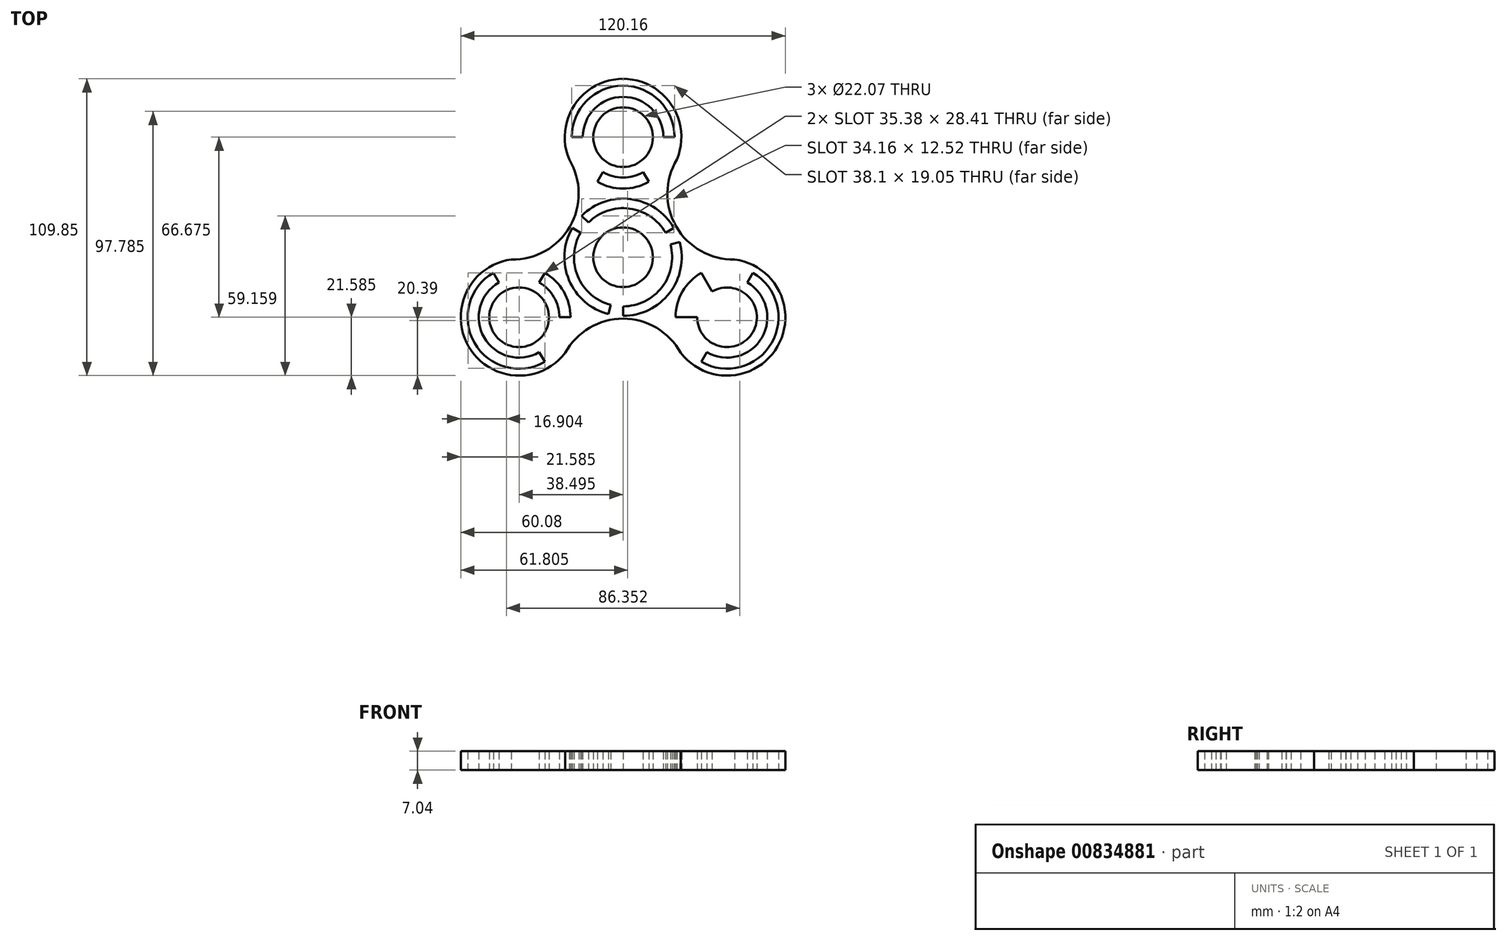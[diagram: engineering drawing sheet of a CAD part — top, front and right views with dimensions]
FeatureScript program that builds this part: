
annotation { "Feature Type Name" : "Feature", "Feature Type Description" : "" }
export const myFeature = defineFeature(function(context is Context, id is Id, definition is map)
    precondition{}
    {
        {
            var Q0;
            Q0=qCreatedBy(makeId("Top.planeOp"),FACE);
            var sketch = newSketch(context, id + "F0", { "sketchPlane" : qUnion([Q0])});
            skCircle(sketch, "E0", {"center": v(0, 0) * mm, "radius": 11.04 * mm});
            skCircle(sketch, "E1", {"center": v(0, 0) * mm, "radius": 14.16 * mm});
            skCircle(sketch, "E2", {"center": v(0, 0) * mm, "radius": 21.71 * mm});
            skLineSegment(sketch, "E3", {"start": v(0, 0) * mm, "end": v(0, 21.71) * mm});
            skLineSegment(sketch, "E4", {"start": v(0, 0) * mm, "end": v(18.8, -10.86) * mm});
            skLineSegment(sketch, "E5", {"start": v(0, 0) * mm, "end": v(-18.8, -10.86) * mm});
            skLineSegment(sketch, "E6", {"start": v(0, 21.71) * mm, "end": v(0, 44.45) * mm});
            skLineSegment(sketch, "E7", {"start": v(18.8, -10.86) * mm, "end": v(38.5, -22.22) * mm});
            skLineSegment(sketch, "E8", {"start": v(-18.8, -10.86) * mm, "end": v(-38.5, -22.22) * mm});
            skLineSegment(sketch, "E9", {"start": v(0, 48.79) * mm, "end": v(0, 44.45) * mm});
            skLineSegment(sketch, "E10", {"start": v(-42.25, -24.4) * mm, "end": v(-38.5, -22.22) * mm});
            skLineSegment(sketch, "E11", {"start": v(42.25, -24.4) * mm, "end": v(38.5, -22.22) * mm});
            skLineSegment(sketch, "E12", {"start": v(-42.25, -24.4) * mm, "end": v(-37.85, -21.85) * mm});
            skLineSegment(sketch, "E13", {"start": v(0, 48.79) * mm, "end": v(0, 43.7) * mm});
            skLineSegment(sketch, "E14", {"start": v(42.25, -24.4) * mm, "end": v(28.65, -16.54) * mm});
            skCircle(sketch, "E15", {"center": v(-38.5, -22.22) * mm, "radius": 11.04 * mm});
            skCircle(sketch, "E16", {"center": v(38.5, -22.22) * mm, "radius": 11.04 * mm});
            skCircle(sketch, "E17", {"center": v(0, 44.45) * mm, "radius": 11.04 * mm});
            skCircle(sketch, "E18", {"center": v(-38.5, -22.22) * mm, "radius": 19.05 * mm});
            skCircle(sketch, "E19", {"center": v(0, 44.45) * mm, "radius": 19.05 * mm});
            skCircle(sketch, "E20", {"center": v(38.5, -22.22) * mm, "radius": 19.05 * mm});
            skLineSegment(sketch, "E21", {"start": v(-38.5, -22.22) * mm, "end": v(-48.02, -5.73) * mm});
            skLineSegment(sketch, "E22", {"start": v(0, 44.45) * mm, "end": v(19.05, 44.45) * mm});
            skLineSegment(sketch, "E23", {"start": v(38.5, -22.22) * mm, "end": v(48.02, -5.73) * mm});
            skLineSegment(sketch, "E24", {"start": v(-38.5, -22.22) * mm, "end": v(-28.97, -38.72) * mm});
            skLineSegment(sketch, "E25", {"start": v(38.5, -22.22) * mm, "end": v(28.97, -38.72) * mm});
            skLineSegment(sketch, "E26", {"start": v(0, 44.45) * mm, "end": v(-19.05, 44.45) * mm});
            skLineSegment(sketch, "E27", {"start": v(0, 0) * mm, "end": v(-18.8, 10.86) * mm});
            skLineSegment(sketch, "E28", {"start": v(-18.8, 10.86) * mm, "end": v(0, 0) * mm});
            skLineSegment(sketch, "E29", {"start": v(0, 0) * mm, "end": v(-10.86, -18.8) * mm});
            skLineSegment(sketch, "E30", {"start": v(-10.86, -18.8) * mm, "end": v(0, 0) * mm});
            skLineSegment(sketch, "E31", {"start": v(0, 0) * mm, "end": v(10.86, -18.8) * mm});
            skLineSegment(sketch, "E32", {"start": v(10.86, -18.8) * mm, "end": v(0, 0) * mm});
            skLineSegment(sketch, "E33", {"start": v(0, 0) * mm, "end": v(10.86, 18.8) * mm});
            skLineSegment(sketch, "E34", {"start": v(10.86, 18.8) * mm, "end": v(0, 0) * mm});
            skLineSegment(sketch, "E35", {"start": v(0, 0) * mm, "end": v(21.71, 0) * mm});
            skLineSegment(sketch, "E36", {"start": v(21.71, 0) * mm, "end": v(0, 0) * mm});
            skLineSegment(sketch, "E37", {"start": v(0, 0) * mm, "end": v(-21.71, 0) * mm});
            skLineSegment(sketch, "E38", {"start": v(-21.71, 0) * mm, "end": v(0, 0) * mm});
            skLineSegment(sketch, "E39", {"start": v(0, 0) * mm, "end": v(-10.86, 18.8) * mm});
            skLineSegment(sketch, "E40", {"start": v(0, 0) * mm, "end": v(18.8, 10.86) * mm});
            skLineSegment(sketch, "E41", {"start": v(0, 0) * mm, "end": v(0, -21.71) * mm});
            skLineSegment(sketch, "E42", {"start": v(0, 0) * mm, "end": v(5.43, 21.02) * mm});
            skPoint(sketch, "E42.endSnap0", {"position": v(5.43, 9.4) * mm});
            skLineSegment(sketch, "E43", {"start": v(0, 0) * mm, "end": v(20.97, 5.62) * mm});
            skLineSegment(sketch, "E44", {"start": v(0, 0) * mm, "end": v(15.35, -15.35) * mm});
            skLineSegment(sketch, "E45", {"start": v(0, 0) * mm, "end": v(-5.43, -21.02) * mm});
            skPoint(sketch, "E45.endSnap0", {"position": v(-5.43, -9.4) * mm});
            skLineSegment(sketch, "E46", {"start": v(0, 0) * mm, "end": v(-20.97, -5.62) * mm});
            skLineSegment(sketch, "E47", {"start": v(0, 0) * mm, "end": v(-15.35, 15.35) * mm});
            skCircle(sketch, "E48", {"center": v(0, 0) * mm, "radius": 24.25 * mm});
            skCircle(sketch, "E49", {"center": v(38.5, -22.22) * mm, "radius": 21.59 * mm});
            skCircle(sketch, "E50", {"center": v(0, 44.45) * mm, "radius": 21.59 * mm});
            skCircle(sketch, "E51", {"center": v(-38.5, -22.22) * mm, "radius": 21.59 * mm});
            skCircle(sketch, "E52", {"center": v(0, 0) * mm, "radius": 18.18 * mm});
            skPoint(sketch, "E53", {"position": v(-19.05, 44.45) * mm});
            skPoint(sketch, "E54", {"position": v(17.11, 36.08) * mm});
            skPoint(sketch, "E55", {"position": v(39.8, -3.22) * mm});
            skPoint(sketch, "E56", {"position": v(22.7, -32.86) * mm});
            skPoint(sketch, "E57", {"position": v(-22.7, -32.86) * mm});
            skPoint(sketch, "E58", {"position": v(-35.27, -0.88) * mm});
            skLineSegment(sketch, "E59", {"start": v(-38.5, -22.22) * mm, "end": v(0, 44.45) * mm});
            skLineSegment(sketch, "E60", {"start": v(0, 44.45) * mm, "end": v(38.5, -22.22) * mm});
            skLineSegment(sketch, "E61", {"start": v(-38.5, -22.22) * mm, "end": v(38.5, -22.22) * mm});
            skLineSegment(sketch, "E62", {"start": v(18.8, 10.86) * mm, "end": v(40.8, 23.56) * mm});
            skLineSegment(sketch, "E63", {"start": v(-18.8, 10.86) * mm, "end": v(-40.8, 23.56) * mm});
            skLineSegment(sketch, "E64", {"start": v(0, -21.71) * mm, "end": v(0, -47.11) * mm});
            skCircle(sketch, "E65", {"center": v(40.8, 23.56) * mm, "radius": 24.38 * mm});
            skCircle(sketch, "E66", {"center": v(0, -47.11) * mm, "radius": 24.38 * mm});
            skCircle(sketch, "E67", {"center": v(-40.8, 23.56) * mm, "radius": 24.38 * mm});
            skCircle(sketch, "E68", {"center": v(-38.5, -22.22) * mm, "radius": 14.92 * mm});
            skCircle(sketch, "E69", {"center": v(38.5, -22.22) * mm, "radius": 14.92 * mm});
            skCircle(sketch, "E70", {"center": v(0, 44.45) * mm, "radius": 14.92 * mm});
            skSolve(sketch);
        }
        {
            var Q0;
            {var subQ0=sQuery(id+"F0.wireOp",EDGE,"E28");var subQ1=sQuery(id+"F0.wireOp",EDGE,"E0");var subQ2=makeQuery(id+"F0.imprint","INTERSECT",VERTEX,{"derivedFrom":[subQ1,subQ0]});Q0=makeQuery(id+"F0.imprint","IMPRINT",FACE,{"disambiguationData":[TD([[makeQuery(id+"F0.imprint","IMPRINT",EDGE,{"disambiguationData":[TD([[subQ2,-1.0]])],"derivedFrom":subQ1}),-1.0]])]});}
            var Q1;
            {var subQ0=sQuery(id+"F0.wireOp",EDGE,"E47");var subQ1=sQuery(id+"F0.wireOp",EDGE,"E0");var subQ2=makeQuery(id+"F0.imprint","INTERSECT",VERTEX,{"derivedFrom":[subQ1,subQ0]});Q1=makeQuery(id+"F0.imprint","IMPRINT",FACE,{"disambiguationData":[TD([[makeQuery(id+"F0.imprint","IMPRINT",EDGE,{"disambiguationData":[TD([[subQ2,-1.0]])],"derivedFrom":subQ1}),-1.0]])]});}
            var Q2;
            {var subQ0=sQuery(id+"F0.wireOp",EDGE,"E39");var subQ1=sQuery(id+"F0.wireOp",EDGE,"E0");var subQ2=makeQuery(id+"F0.imprint","INTERSECT",VERTEX,{"derivedFrom":[subQ1,subQ0]});Q2=makeQuery(id+"F0.imprint","IMPRINT",FACE,{"disambiguationData":[TD([[makeQuery(id+"F0.imprint","IMPRINT",EDGE,{"disambiguationData":[TD([[subQ2,-1.0]])],"derivedFrom":subQ1}),-1.0]])]});}
            var Q3;
            {var subQ0=sQuery(id+"F0.wireOp",EDGE,"E3");var subQ1=sQuery(id+"F0.wireOp",EDGE,"E0");var subQ2=makeQuery(id+"F0.imprint","INTERSECT",VERTEX,{"derivedFrom":[subQ1,subQ0]});Q3=makeQuery(id+"F0.imprint","IMPRINT",FACE,{"disambiguationData":[TD([[makeQuery(id+"F0.imprint","IMPRINT",EDGE,{"disambiguationData":[TD([[subQ2,-1.0]])],"derivedFrom":subQ1}),-1.0]])]});}
            var Q4;
            {var subQ0=sQuery(id+"F0.wireOp",EDGE,"E42");var subQ1=sQuery(id+"F0.wireOp",EDGE,"E0");var subQ2=makeQuery(id+"F0.imprint","INTERSECT",VERTEX,{"derivedFrom":[subQ1,subQ0]});Q4=makeQuery(id+"F0.imprint","IMPRINT",FACE,{"disambiguationData":[TD([[makeQuery(id+"F0.imprint","IMPRINT",EDGE,{"disambiguationData":[TD([[subQ2,-1.0]])],"derivedFrom":subQ1}),-1.0]])]});}
            var Q5;
            {var subQ0=sQuery(id+"F0.wireOp",EDGE,"E34");var subQ1=sQuery(id+"F0.wireOp",EDGE,"E0");var subQ2=makeQuery(id+"F0.imprint","INTERSECT",VERTEX,{"derivedFrom":[subQ1,subQ0]});Q5=makeQuery(id+"F0.imprint","IMPRINT",FACE,{"disambiguationData":[TD([[makeQuery(id+"F0.imprint","IMPRINT",EDGE,{"disambiguationData":[TD([[subQ2,-1.0]])],"derivedFrom":subQ1}),-1.0]])]});}
            var Q6;
            {var subQ0=sQuery(id+"F0.wireOp",EDGE,"E40");var subQ1=sQuery(id+"F0.wireOp",EDGE,"E0");var subQ2=makeQuery(id+"F0.imprint","INTERSECT",VERTEX,{"derivedFrom":[subQ1,subQ0]});Q6=makeQuery(id+"F0.imprint","IMPRINT",FACE,{"disambiguationData":[TD([[makeQuery(id+"F0.imprint","IMPRINT",EDGE,{"disambiguationData":[TD([[subQ2,-1.0]])],"derivedFrom":subQ1}),-1.0]])]});}
            var Q7;
            {var subQ0=sQuery(id+"F0.wireOp",EDGE,"E43");var subQ1=sQuery(id+"F0.wireOp",EDGE,"E0");var subQ2=makeQuery(id+"F0.imprint","INTERSECT",VERTEX,{"derivedFrom":[subQ1,subQ0]});Q7=makeQuery(id+"F0.imprint","IMPRINT",FACE,{"disambiguationData":[TD([[makeQuery(id+"F0.imprint","IMPRINT",EDGE,{"disambiguationData":[TD([[subQ2,-1.0]])],"derivedFrom":subQ1}),-1.0]])]});}
            var Q8;
            {var subQ0=sQuery(id+"F0.wireOp",EDGE,"E43");var subQ1=sQuery(id+"F0.wireOp",EDGE,"E0");var subQ2=makeQuery(id+"F0.imprint","INTERSECT",VERTEX,{"derivedFrom":[subQ1,subQ0]});Q8=makeQuery(id+"F0.imprint","IMPRINT",FACE,{"disambiguationData":[TD([[makeQuery(id+"F0.imprint","IMPRINT",EDGE,{"disambiguationData":[TD([[subQ2,1.0]])],"derivedFrom":subQ1}),-1.0]])]});}
            var Q9;
            {var subQ0=sQuery(id+"F0.wireOp",EDGE,"E36");var subQ1=sQuery(id+"F0.wireOp",EDGE,"E0");var subQ2=makeQuery(id+"F0.imprint","INTERSECT",VERTEX,{"derivedFrom":[subQ1,subQ0]});Q9=makeQuery(id+"F0.imprint","IMPRINT",FACE,{"disambiguationData":[TD([[makeQuery(id+"F0.imprint","IMPRINT",EDGE,{"disambiguationData":[TD([[subQ2,1.0]])],"derivedFrom":subQ1}),-1.0]])]});}
            var Q10;
            {var subQ0=sQuery(id+"F0.wireOp",EDGE,"E44");var subQ1=sQuery(id+"F0.wireOp",EDGE,"E0");var subQ2=makeQuery(id+"F0.imprint","INTERSECT",VERTEX,{"derivedFrom":[subQ1,subQ0]});Q10=makeQuery(id+"F0.imprint","IMPRINT",FACE,{"disambiguationData":[TD([[makeQuery(id+"F0.imprint","IMPRINT",EDGE,{"disambiguationData":[TD([[subQ2,-1.0]])],"derivedFrom":subQ1}),-1.0]])]});}
            var Q11;
            {var subQ0=sQuery(id+"F0.wireOp",EDGE,"E32");var subQ1=sQuery(id+"F0.wireOp",EDGE,"E0");var subQ2=makeQuery(id+"F0.imprint","INTERSECT",VERTEX,{"derivedFrom":[subQ1,subQ0]});Q11=makeQuery(id+"F0.imprint","IMPRINT",FACE,{"disambiguationData":[TD([[makeQuery(id+"F0.imprint","IMPRINT",EDGE,{"disambiguationData":[TD([[subQ2,-1.0]])],"derivedFrom":subQ1}),-1.0]])]});}
            var Q12;
            {var subQ0=sQuery(id+"F0.wireOp",EDGE,"E41");var subQ1=sQuery(id+"F0.wireOp",EDGE,"E0");var subQ2=makeQuery(id+"F0.imprint","INTERSECT",VERTEX,{"derivedFrom":[subQ1,subQ0]});Q12=makeQuery(id+"F0.imprint","IMPRINT",FACE,{"disambiguationData":[TD([[makeQuery(id+"F0.imprint","IMPRINT",EDGE,{"disambiguationData":[TD([[subQ2,-1.0]])],"derivedFrom":subQ1}),-1.0]])]});}
            var Q13;
            {var subQ0=sQuery(id+"F0.wireOp",EDGE,"E30");var subQ1=sQuery(id+"F0.wireOp",EDGE,"E0");var subQ2=makeQuery(id+"F0.imprint","INTERSECT",VERTEX,{"derivedFrom":[subQ1,subQ0]});Q13=makeQuery(id+"F0.imprint","IMPRINT",FACE,{"disambiguationData":[TD([[makeQuery(id+"F0.imprint","IMPRINT",EDGE,{"disambiguationData":[TD([[subQ2,-1.0]])],"derivedFrom":subQ1}),-1.0]])]});}
            var Q14;
            {var subQ0=sQuery(id+"F0.wireOp",EDGE,"E45");var subQ1=sQuery(id+"F0.wireOp",EDGE,"E0");var subQ2=makeQuery(id+"F0.imprint","INTERSECT",VERTEX,{"derivedFrom":[subQ1,subQ0]});Q14=makeQuery(id+"F0.imprint","IMPRINT",FACE,{"disambiguationData":[TD([[makeQuery(id+"F0.imprint","IMPRINT",EDGE,{"disambiguationData":[TD([[subQ2,-1.0]])],"derivedFrom":subQ1}),-1.0]])]});}
            var Q15;
            {var subQ0=sQuery(id+"F0.wireOp",EDGE,"E5");var subQ1=sQuery(id+"F0.wireOp",EDGE,"E0");var subQ2=makeQuery(id+"F0.imprint","INTERSECT",VERTEX,{"derivedFrom":[subQ1,subQ0]});Q15=makeQuery(id+"F0.imprint","IMPRINT",FACE,{"disambiguationData":[TD([[makeQuery(id+"F0.imprint","IMPRINT",EDGE,{"disambiguationData":[TD([[subQ2,-1.0]])],"derivedFrom":subQ1}),-1.0]])]});}
            var Q16;
            {var subQ0=sQuery(id+"F0.wireOp",EDGE,"E46");var subQ1=sQuery(id+"F0.wireOp",EDGE,"E0");var subQ2=makeQuery(id+"F0.imprint","INTERSECT",VERTEX,{"derivedFrom":[subQ1,subQ0]});Q16=makeQuery(id+"F0.imprint","IMPRINT",FACE,{"disambiguationData":[TD([[makeQuery(id+"F0.imprint","IMPRINT",EDGE,{"disambiguationData":[TD([[subQ2,-1.0]])],"derivedFrom":subQ1}),-1.0]])]});}
            var Q17;
            {var subQ0=sQuery(id+"F0.wireOp",EDGE,"E38");var subQ1=sQuery(id+"F0.wireOp",EDGE,"E0");var subQ2=makeQuery(id+"F0.imprint","INTERSECT",VERTEX,{"derivedFrom":[subQ1,subQ0]});Q17=makeQuery(id+"F0.imprint","IMPRINT",FACE,{"disambiguationData":[TD([[makeQuery(id+"F0.imprint","IMPRINT",EDGE,{"disambiguationData":[TD([[subQ2,-1.0]])],"derivedFrom":subQ1}),-1.0]])]});}
            var Q18;
            {var subQ1=sQuery(id+"F0.wireOp",EDGE,"E2");var subQ3=makeQuery(id+"F0.imprint","INTERSECT",VERTEX,{"derivedFrom":[subQ1,sQuery(id+"F0.wireOp",EDGE,"E36")]});Q18=makeQuery(id+"F0.imprint","IMPRINT",FACE,{"disambiguationData":[TD([[makeQuery(id+"F0.imprint","IMPRINT",EDGE,{"disambiguationData":[TD([[subQ3,-1.0]])],"derivedFrom":subQ1}),-1.0]])]});}
            var Q19;
            {var subQ1=sQuery(id+"F0.wireOp",EDGE,"E2");var subQ4=makeQuery(id+"F0.imprint","INTERSECT",VERTEX,{"derivedFrom":[subQ1,sQuery(id+"F0.wireOp",EDGE,"E39")]});Q19=makeQuery(id+"F0.imprint","IMPRINT",FACE,{"disambiguationData":[TD([[makeQuery(id+"F0.imprint","IMPRINT",EDGE,{"disambiguationData":[TD([[subQ4,-1.0]])],"derivedFrom":subQ1}),-1.0]])]});}
            var Q20;
            {var subQ1=sQuery(id+"F0.wireOp",EDGE,"E2");var subQ4=makeQuery(id+"F0.imprint","INTERSECT",VERTEX,{"derivedFrom":[subQ1,sQuery(id+"F0.wireOp",EDGE,"E30")]});Q20=makeQuery(id+"F0.imprint","IMPRINT",FACE,{"disambiguationData":[TD([[makeQuery(id+"F0.imprint","IMPRINT",EDGE,{"disambiguationData":[TD([[subQ4,-1.0]])],"derivedFrom":subQ1}),-1.0]])]});}
            var Q21;
            {var subQ1=sQuery(id+"F0.wireOp",EDGE,"E2");var subQ5=makeQuery(id+"F0.imprint","INTERSECT",VERTEX,{"derivedFrom":[subQ1,sQuery(id+"F0.wireOp",EDGE,"E32")]});Q21=makeQuery(id+"F0.imprint","IMPRINT",FACE,{"disambiguationData":[TD([[makeQuery(id+"F0.imprint","IMPRINT",EDGE,{"disambiguationData":[TD([[subQ5,-1.0]])],"derivedFrom":subQ1}),-1.0]])]});}
            var Q22;
            {var subQ0=sQuery(id+"F0.wireOp",EDGE,"E23");var subQ1=sQuery(id+"F0.wireOp",EDGE,"E16");var subQ2=makeQuery(id+"F0.imprint","INTERSECT",VERTEX,{"derivedFrom":[subQ1,subQ0]});Q22=makeQuery(id+"F0.imprint","IMPRINT",FACE,{"disambiguationData":[TD([[makeQuery(id+"F0.imprint","IMPRINT",EDGE,{"disambiguationData":[TD([[subQ2,1.0]])],"derivedFrom":subQ1}),-1.0]])]});}
            var Q23;
            {var subQ1=sQuery(id+"F0.wireOp",EDGE,"E14");var subQ7=sQuery(id+"F0.wireOp",EDGE,"E7");var subQ8=makeQuery(id+"F0.imprint","INTERSECT",VERTEX,{"derivedFrom":[subQ7,subQ1]});Q23=makeQuery(id+"F0.imprint","IMPRINT",FACE,{"disambiguationData":[TD([[makeQuery(id+"F0.imprint","IMPRINT",EDGE,{"disambiguationData":[TD([[subQ8,1.0]])],"derivedFrom":subQ7}),1.0]])]});}
            var Q24;
            {var subQ5=sQuery(id+"F0.wireOp",EDGE,"E14");var subQ7=sQuery(id+"F0.wireOp",EDGE,"E7");var subQ8=makeQuery(id+"F0.imprint","INTERSECT",VERTEX,{"derivedFrom":[subQ7,subQ5]});Q24=makeQuery(id+"F0.imprint","IMPRINT",FACE,{"disambiguationData":[TD([[makeQuery(id+"F0.imprint","IMPRINT",EDGE,{"disambiguationData":[TD([[subQ8,1.0]])],"derivedFrom":subQ7}),-1.0]])]});}
            var Q25;
            {var subQ0=sQuery(id+"F0.wireOp",EDGE,"E21");var subQ1=sQuery(id+"F0.wireOp",EDGE,"E15");var subQ2=makeQuery(id+"F0.imprint","INTERSECT",VERTEX,{"derivedFrom":[subQ1,subQ0]});Q25=makeQuery(id+"F0.imprint","IMPRINT",FACE,{"disambiguationData":[TD([[makeQuery(id+"F0.imprint","IMPRINT",EDGE,{"disambiguationData":[TD([[subQ2,-1.0]])],"derivedFrom":subQ1}),-1.0]])]});}
            var Q26;
            {var subQ0=sQuery(id+"F0.wireOp",EDGE,"E26");var subQ1=sQuery(id+"F0.wireOp",EDGE,"E17");var subQ2=makeQuery(id+"F0.imprint","INTERSECT",VERTEX,{"derivedFrom":[subQ1,subQ0]});Q26=makeQuery(id+"F0.imprint","IMPRINT",FACE,{"disambiguationData":[TD([[makeQuery(id+"F0.imprint","IMPRINT",EDGE,{"disambiguationData":[TD([[subQ2,1.0]])],"derivedFrom":subQ1}),-1.0]])]});}
            var Q27;
            {var subQ5=sQuery(id+"F0.wireOp",EDGE,"E19");var subQ8=makeQuery(id+"F0.imprint","INTERSECT",VERTEX,{"derivedFrom":[subQ5,sQuery(id+"F0.wireOp",EDGE,"E22")]});Q27=makeQuery(id+"F0.imprint","IMPRINT",FACE,{"disambiguationData":[TD([[makeQuery(id+"F0.imprint","IMPRINT",EDGE,{"disambiguationData":[TD([[subQ8,-1.0]])],"derivedFrom":subQ5}),-1.0]])]});}
            var Q28;
            {var subQ0=sQuery(id+"F0.wireOp",EDGE,"E20");var subQ1=makeQuery(id+"F0.imprint","INTERSECT",VERTEX,{"derivedFrom":[subQ0,sQuery(id+"F0.wireOp",EDGE,"E23")]});Q28=makeQuery(id+"F0.imprint","IMPRINT",FACE,{"disambiguationData":[TD([[makeQuery(id+"F0.imprint","IMPRINT",EDGE,{"disambiguationData":[TD([[subQ1,-1.0]])],"derivedFrom":subQ0}),-1.0]])]});}
            var Q29;
            {var subQ0=sQuery(id+"F0.wireOp",EDGE,"E51");var subQ1=sQuery(id+"F0.wireOp",EDGE,"E8");var subQ2=makeQuery(id+"F0.imprint","INTERSECT",VERTEX,{"derivedFrom":[subQ1,subQ0]});Q29=makeQuery(id+"F0.imprint","IMPRINT",FACE,{"disambiguationData":[TD([[makeQuery(id+"F0.imprint","IMPRINT",EDGE,{"disambiguationData":[TD([[subQ2,-1.0]])],"derivedFrom":subQ1}),1.0]])]});}
            var Q30;
            {var subQ0=sQuery(id+"F0.wireOp",EDGE,"E51");var subQ1=sQuery(id+"F0.wireOp",EDGE,"E8");var subQ2=makeQuery(id+"F0.imprint","INTERSECT",VERTEX,{"derivedFrom":[subQ1,subQ0]});Q30=makeQuery(id+"F0.imprint","IMPRINT",FACE,{"disambiguationData":[TD([[makeQuery(id+"F0.imprint","IMPRINT",EDGE,{"disambiguationData":[TD([[subQ2,-1.0]])],"derivedFrom":subQ1}),-1.0]])]});}
            var Q31;
            {var subQ1=sQuery(id+"F0.wireOp",EDGE,"E48");var subQ6=sQuery(id+"F0.wireOp",EDGE,"E6");var subQ9=makeQuery(id+"F0.imprint","INTERSECT",VERTEX,{"derivedFrom":[subQ6,subQ1]});Q31=makeQuery(id+"F0.imprint","IMPRINT",FACE,{"disambiguationData":[TD([[makeQuery(id+"F0.imprint","IMPRINT",EDGE,{"disambiguationData":[TD([[subQ9,-1.0]])],"derivedFrom":subQ6}),1.0]])]});}
            var Q32;
            {var subQ0=sQuery(id+"F0.wireOp",EDGE,"E50");var subQ1=sQuery(id+"F0.wireOp",EDGE,"E6");var subQ2=makeQuery(id+"F0.imprint","INTERSECT",VERTEX,{"derivedFrom":[subQ1,subQ0]});Q32=makeQuery(id+"F0.imprint","IMPRINT",FACE,{"disambiguationData":[TD([[makeQuery(id+"F0.imprint","IMPRINT",EDGE,{"disambiguationData":[TD([[subQ2,-1.0]])],"derivedFrom":subQ1}),-1.0]])]});}
            var Q33;
            {var subQ0=sQuery(id+"F0.wireOp",EDGE,"E48");var subQ1=sQuery(id+"F0.wireOp",EDGE,"E6");var subQ2=makeQuery(id+"F0.imprint","INTERSECT",VERTEX,{"derivedFrom":[subQ1,subQ0]});Q33=makeQuery(id+"F0.imprint","IMPRINT",FACE,{"disambiguationData":[TD([[makeQuery(id+"F0.imprint","IMPRINT",EDGE,{"disambiguationData":[TD([[subQ2,-1.0]])],"derivedFrom":subQ1}),-1.0]])]});}
            var Q34;
            {var subQ0=sQuery(id+"F0.wireOp",EDGE,"E50");var subQ1=sQuery(id+"F0.wireOp",EDGE,"E6");var subQ2=makeQuery(id+"F0.imprint","INTERSECT",VERTEX,{"derivedFrom":[subQ1,subQ0]});Q34=makeQuery(id+"F0.imprint","IMPRINT",FACE,{"disambiguationData":[TD([[makeQuery(id+"F0.imprint","IMPRINT",EDGE,{"disambiguationData":[TD([[subQ2,-1.0]])],"derivedFrom":subQ1}),1.0]])]});}
            var Q35;
            {var subQ1=sQuery(id+"F0.wireOp",EDGE,"E48");var subQ5=sQuery(id+"F0.wireOp",EDGE,"E7");var subQ6=makeQuery(id+"F0.imprint","INTERSECT",VERTEX,{"derivedFrom":[subQ5,subQ1]});Q35=makeQuery(id+"F0.imprint","IMPRINT",FACE,{"disambiguationData":[TD([[makeQuery(id+"F0.imprint","IMPRINT",EDGE,{"disambiguationData":[TD([[subQ6,-1.0]])],"derivedFrom":subQ5}),1.0]])]});}
            var Q36;
            {var subQ0=sQuery(id+"F0.wireOp",EDGE,"E49");var subQ1=sQuery(id+"F0.wireOp",EDGE,"E7");var subQ2=makeQuery(id+"F0.imprint","INTERSECT",VERTEX,{"derivedFrom":[subQ1,subQ0]});Q36=makeQuery(id+"F0.imprint","IMPRINT",FACE,{"disambiguationData":[TD([[makeQuery(id+"F0.imprint","IMPRINT",EDGE,{"disambiguationData":[TD([[subQ2,-1.0]])],"derivedFrom":subQ1}),1.0]])]});}
            var Q37;
            {var subQ0=sQuery(id+"F0.wireOp",EDGE,"E50");var subQ1=sQuery(id+"F0.wireOp",EDGE,"E48");var subQ2=makeQuery(id+"F0.imprint","INTERSECT",VERTEX,{"disambiguationData":[OD(1.0)],"derivedFrom":[subQ1,subQ0]});Q37=makeQuery(id+"F0.imprint","IMPRINT",FACE,{"disambiguationData":[TD([[makeQuery(id+"F0.imprint","IMPRINT",EDGE,{"disambiguationData":[TD([[subQ2,-1.0]])],"derivedFrom":subQ1}),-1.0]])]});}
            var Q38;
            {var subQ1=sQuery(id+"F0.wireOp",EDGE,"E48");var subQ5=sQuery(id+"F0.wireOp",EDGE,"E8");var subQ6=makeQuery(id+"F0.imprint","INTERSECT",VERTEX,{"derivedFrom":[subQ5,subQ1]});Q38=makeQuery(id+"F0.imprint","IMPRINT",FACE,{"disambiguationData":[TD([[makeQuery(id+"F0.imprint","IMPRINT",EDGE,{"disambiguationData":[TD([[subQ6,-1.0]])],"derivedFrom":subQ5}),-1.0]])]});}
            var Q39;
            {var subQ5=sQuery(id+"F0.wireOp",EDGE,"E18");var subQ9=makeQuery(id+"F0.imprint","INTERSECT",VERTEX,{"derivedFrom":[subQ5,sQuery(id+"F0.wireOp",EDGE,"E21")]});Q39=makeQuery(id+"F0.imprint","IMPRINT",FACE,{"disambiguationData":[TD([[makeQuery(id+"F0.imprint","IMPRINT",EDGE,{"disambiguationData":[TD([[subQ9,1.0]])],"derivedFrom":subQ5}),-1.0]])]});}
            var Q40;
            {var subQ0=sQuery(id+"F0.wireOp",EDGE,"E51");var subQ1=sQuery(id+"F0.wireOp",EDGE,"E48");var subQ2=makeQuery(id+"F0.imprint","INTERSECT",VERTEX,{"disambiguationData":[OD(1.0)],"derivedFrom":[subQ1,subQ0]});Q40=makeQuery(id+"F0.imprint","IMPRINT",FACE,{"disambiguationData":[TD([[makeQuery(id+"F0.imprint","IMPRINT",EDGE,{"disambiguationData":[TD([[subQ2,-1.0]])],"derivedFrom":subQ1}),-1.0]])]});}
            var Q41;
            {var subQ0=sQuery(id+"F0.wireOp",EDGE,"E48");var subQ1=sQuery(id+"F0.wireOp",EDGE,"E7");var subQ2=makeQuery(id+"F0.imprint","INTERSECT",VERTEX,{"derivedFrom":[subQ1,subQ0]});Q41=makeQuery(id+"F0.imprint","IMPRINT",FACE,{"disambiguationData":[TD([[makeQuery(id+"F0.imprint","IMPRINT",EDGE,{"disambiguationData":[TD([[subQ2,-1.0]])],"derivedFrom":subQ1}),-1.0]])]});}
            var Q42;
            {var subQ0=sQuery(id+"F0.wireOp",EDGE,"E49");var subQ1=sQuery(id+"F0.wireOp",EDGE,"E7");var subQ2=makeQuery(id+"F0.imprint","INTERSECT",VERTEX,{"derivedFrom":[subQ1,subQ0]});Q42=makeQuery(id+"F0.imprint","IMPRINT",FACE,{"disambiguationData":[TD([[makeQuery(id+"F0.imprint","IMPRINT",EDGE,{"disambiguationData":[TD([[subQ2,-1.0]])],"derivedFrom":subQ1}),-1.0]])]});}
            var Q43;
            {var subQ1=sQuery(id+"F0.wireOp",EDGE,"E48");var subQ6=sQuery(id+"F0.wireOp",EDGE,"E8");var subQ9=makeQuery(id+"F0.imprint","INTERSECT",VERTEX,{"derivedFrom":[subQ6,subQ1]});Q43=makeQuery(id+"F0.imprint","IMPRINT",FACE,{"disambiguationData":[TD([[makeQuery(id+"F0.imprint","IMPRINT",EDGE,{"disambiguationData":[TD([[subQ9,-1.0]])],"derivedFrom":subQ6}),1.0]])]});}
            var Q44;
            {var subQ0=sQuery(id+"F0.wireOp",EDGE,"E59");var subQ1=sQuery(id+"F0.wireOp",EDGE,"E48");var subQ2=makeQuery(id+"F0.imprint","INTERSECT",VERTEX,{"disambiguationData":[OD(0.0)],"derivedFrom":[subQ1,subQ0]});Q44=makeQuery(id+"F0.imprint","IMPRINT",FACE,{"disambiguationData":[TD([[makeQuery(id+"F0.imprint","IMPRINT",EDGE,{"disambiguationData":[TD([[subQ2,-1.0]])],"derivedFrom":subQ1}),-1.0]])]});}
            var Q45;
            {var subQ0=sQuery(id+"F0.wireOp",EDGE,"E65");var subQ1=sQuery(id+"F0.wireOp",EDGE,"E48");var subQ2=makeQuery(id+"F0.imprint","INTERSECT",VERTEX,{"disambiguationData":[OD(1.0)],"derivedFrom":[subQ1,subQ0]});Q45=makeQuery(id+"F0.imprint","IMPRINT",FACE,{"disambiguationData":[TD([[makeQuery(id+"F0.imprint","IMPRINT",EDGE,{"disambiguationData":[TD([[subQ2,-1.0]])],"derivedFrom":subQ1}),-1.0]])]});}
            var Q46;
            {var subQ0=sQuery(id+"F0.wireOp",EDGE,"E65");var subQ1=sQuery(id+"F0.wireOp",EDGE,"E48");var subQ2=makeQuery(id+"F0.imprint","INTERSECT",VERTEX,{"disambiguationData":[OD(0.0)],"derivedFrom":[subQ1,subQ0]});Q46=makeQuery(id+"F0.imprint","IMPRINT",FACE,{"disambiguationData":[TD([[makeQuery(id+"F0.imprint","IMPRINT",EDGE,{"disambiguationData":[TD([[subQ2,1.0]])],"derivedFrom":subQ1}),-1.0]])]});}
            var Q47;
            {var subQ1=sQuery(id+"F0.wireOp",EDGE,"E2");var subQ7=makeQuery(id+"F0.imprint","INTERSECT",VERTEX,{"derivedFrom":[subQ1,sQuery(id+"F0.wireOp",EDGE,"E38")]});Q47=makeQuery(id+"F0.imprint","IMPRINT",FACE,{"disambiguationData":[TD([[makeQuery(id+"F0.imprint","IMPRINT",EDGE,{"disambiguationData":[TD([[subQ7,-1.0]])],"derivedFrom":subQ1}),-1.0]])]});}
            var Q48;
            {var subQ0=sQuery(id+"F0.wireOp",EDGE,"E67");var subQ1=sQuery(id+"F0.wireOp",EDGE,"E48");var subQ2=makeQuery(id+"F0.imprint","INTERSECT",VERTEX,{"disambiguationData":[OD(1.0)],"derivedFrom":[subQ1,subQ0]});Q48=makeQuery(id+"F0.imprint","IMPRINT",FACE,{"disambiguationData":[TD([[makeQuery(id+"F0.imprint","IMPRINT",EDGE,{"disambiguationData":[TD([[subQ2,-1.0]])],"derivedFrom":subQ1}),1.0]])]});}
            var Q49;
            {var subQ0=sQuery(id+"F0.wireOp",EDGE,"E59");var subQ1=sQuery(id+"F0.wireOp",EDGE,"E48");var subQ2=makeQuery(id+"F0.imprint","INTERSECT",VERTEX,{"disambiguationData":[OD(0.0)],"derivedFrom":[subQ1,subQ0]});Q49=makeQuery(id+"F0.imprint","IMPRINT",FACE,{"disambiguationData":[TD([[makeQuery(id+"F0.imprint","IMPRINT",EDGE,{"disambiguationData":[TD([[subQ2,-1.0]])],"derivedFrom":subQ1}),1.0]])]});}
            var Q50;
            {var subQ0=sQuery(id+"F0.wireOp",EDGE,"E67");var subQ1=sQuery(id+"F0.wireOp",EDGE,"E48");var subQ2=makeQuery(id+"F0.imprint","INTERSECT",VERTEX,{"disambiguationData":[OD(1.0)],"derivedFrom":[subQ1,subQ0]});Q50=makeQuery(id+"F0.imprint","IMPRINT",FACE,{"disambiguationData":[TD([[makeQuery(id+"F0.imprint","IMPRINT",EDGE,{"disambiguationData":[TD([[subQ2,-1.0]])],"derivedFrom":subQ1}),-1.0]])]});}
            var Q51;
            {var subQ0=sQuery(id+"F0.wireOp",EDGE,"E59");var subQ1=sQuery(id+"F0.wireOp",EDGE,"E48");var subQ2=makeQuery(id+"F0.imprint","INTERSECT",VERTEX,{"disambiguationData":[OD(1.0)],"derivedFrom":[subQ1,subQ0]});Q51=makeQuery(id+"F0.imprint","IMPRINT",FACE,{"disambiguationData":[TD([[makeQuery(id+"F0.imprint","IMPRINT",EDGE,{"disambiguationData":[TD([[subQ2,-1.0]])],"derivedFrom":subQ1}),-1.0]])]});}
            var Q52;
            {var subQ0=sQuery(id+"F0.wireOp",EDGE,"E61");var subQ1=sQuery(id+"F0.wireOp",EDGE,"E48");var subQ2=makeQuery(id+"F0.imprint","INTERSECT",VERTEX,{"disambiguationData":[OD(0.0)],"derivedFrom":[subQ1,subQ0]});Q52=makeQuery(id+"F0.imprint","IMPRINT",FACE,{"disambiguationData":[TD([[makeQuery(id+"F0.imprint","IMPRINT",EDGE,{"disambiguationData":[TD([[subQ2,-1.0]])],"derivedFrom":subQ1}),1.0]])]});}
            var Q53;
            {var subQ0=sQuery(id+"F0.wireOp",EDGE,"E66");var subQ1=sQuery(id+"F0.wireOp",EDGE,"E48");var subQ2=makeQuery(id+"F0.imprint","INTERSECT",VERTEX,{"disambiguationData":[OD(1.0)],"derivedFrom":[subQ1,subQ0]});Q53=makeQuery(id+"F0.imprint","IMPRINT",FACE,{"disambiguationData":[TD([[makeQuery(id+"F0.imprint","IMPRINT",EDGE,{"disambiguationData":[TD([[subQ2,-1.0]])],"derivedFrom":subQ1}),1.0]])]});}
            var Q54;
            {var subQ0=sQuery(id+"F0.wireOp",EDGE,"E60");var subQ1=sQuery(id+"F0.wireOp",EDGE,"E48");var subQ2=makeQuery(id+"F0.imprint","INTERSECT",VERTEX,{"disambiguationData":[OD(0.0)],"derivedFrom":[subQ1,subQ0]});Q54=makeQuery(id+"F0.imprint","IMPRINT",FACE,{"disambiguationData":[TD([[makeQuery(id+"F0.imprint","IMPRINT",EDGE,{"disambiguationData":[TD([[subQ2,1.0]])],"derivedFrom":subQ1}),-1.0]])]});}
            var Q55;
            {var subQ0=sQuery(id+"F0.wireOp",EDGE,"E65");var subQ1=sQuery(id+"F0.wireOp",EDGE,"E48");var subQ2=makeQuery(id+"F0.imprint","INTERSECT",VERTEX,{"disambiguationData":[OD(0.0)],"derivedFrom":[subQ1,subQ0]});Q55=makeQuery(id+"F0.imprint","IMPRINT",FACE,{"disambiguationData":[TD([[makeQuery(id+"F0.imprint","IMPRINT",EDGE,{"disambiguationData":[TD([[subQ2,1.0]])],"derivedFrom":subQ1}),1.0]])]});}
            var Q56;
            {var subQ0=sQuery(id+"F0.wireOp",EDGE,"E65");var subQ1=sQuery(id+"F0.wireOp",EDGE,"E48");var subQ2=makeQuery(id+"F0.imprint","INTERSECT",VERTEX,{"disambiguationData":[OD(1.0)],"derivedFrom":[subQ1,subQ0]});Q56=makeQuery(id+"F0.imprint","IMPRINT",FACE,{"disambiguationData":[TD([[makeQuery(id+"F0.imprint","IMPRINT",EDGE,{"disambiguationData":[TD([[subQ2,-1.0]])],"derivedFrom":subQ1}),1.0]])]});}
            var Q57;
            {var subQ1=sQuery(id+"F0.wireOp",EDGE,"E2");var subQ6=makeQuery(id+"F0.imprint","INTERSECT",VERTEX,{"derivedFrom":[subQ1,sQuery(id+"F0.wireOp",EDGE,"E34")]});Q57=makeQuery(id+"F0.imprint","IMPRINT",FACE,{"disambiguationData":[TD([[makeQuery(id+"F0.imprint","IMPRINT",EDGE,{"disambiguationData":[TD([[subQ6,-1.0]])],"derivedFrom":subQ1}),-1.0]])]});}
            var Q58;
            {var subQ0=sQuery(id+"F0.wireOp",EDGE,"E60");var subQ1=sQuery(id+"F0.wireOp",EDGE,"E48");var subQ2=makeQuery(id+"F0.imprint","INTERSECT",VERTEX,{"disambiguationData":[OD(1.0)],"derivedFrom":[subQ1,subQ0]});Q58=makeQuery(id+"F0.imprint","IMPRINT",FACE,{"disambiguationData":[TD([[makeQuery(id+"F0.imprint","IMPRINT",EDGE,{"disambiguationData":[TD([[subQ2,-1.0]])],"derivedFrom":subQ1}),-1.0]])]});}
            var Q59;
            {var subQ0=sQuery(id+"F0.wireOp",EDGE,"E61");var subQ1=sQuery(id+"F0.wireOp",EDGE,"E48");var subQ2=makeQuery(id+"F0.imprint","INTERSECT",VERTEX,{"disambiguationData":[OD(0.0)],"derivedFrom":[subQ1,subQ0]});Q59=makeQuery(id+"F0.imprint","IMPRINT",FACE,{"disambiguationData":[TD([[makeQuery(id+"F0.imprint","IMPRINT",EDGE,{"disambiguationData":[TD([[subQ2,-1.0]])],"derivedFrom":subQ1}),-1.0]])]});}
            var Q60;
            {var subQ0=sQuery(id+"F0.wireOp",EDGE,"E66");var subQ1=sQuery(id+"F0.wireOp",EDGE,"E48");var subQ2=makeQuery(id+"F0.imprint","INTERSECT",VERTEX,{"disambiguationData":[OD(1.0)],"derivedFrom":[subQ1,subQ0]});Q60=makeQuery(id+"F0.imprint","IMPRINT",FACE,{"disambiguationData":[TD([[makeQuery(id+"F0.imprint","IMPRINT",EDGE,{"disambiguationData":[TD([[subQ2,-1.0]])],"derivedFrom":subQ1}),-1.0]])]});}
            var Q61;
            {var subQ0=sQuery(id+"F0.wireOp",EDGE,"E61");var subQ1=sQuery(id+"F0.wireOp",EDGE,"E48");var subQ2=makeQuery(id+"F0.imprint","INTERSECT",VERTEX,{"disambiguationData":[OD(1.0)],"derivedFrom":[subQ1,subQ0]});Q61=makeQuery(id+"F0.imprint","IMPRINT",FACE,{"disambiguationData":[TD([[makeQuery(id+"F0.imprint","IMPRINT",EDGE,{"disambiguationData":[TD([[subQ2,-1.0]])],"derivedFrom":subQ1}),-1.0]])]});}
            var Q62;
            {var subQ1=sQuery(id+"F0.wireOp",EDGE,"E2");var subQ3=sQuery(id+"F0.wireOp",EDGE,"E38");var subQ4=makeQuery(id+"F0.imprint","INTERSECT",VERTEX,{"derivedFrom":[subQ1,subQ3]});Q62=makeQuery(id+"F0.imprint","IMPRINT",FACE,{"disambiguationData":[TD([[makeQuery(id+"F0.imprint","IMPRINT",EDGE,{"disambiguationData":[TD([[subQ4,-1.0]])],"derivedFrom":subQ3}),1.0]])]});}
            var Q63;
            {var subQ1=sQuery(id+"F0.wireOp",EDGE,"E2");var subQ3=sQuery(id+"F0.wireOp",EDGE,"E47");var subQ4=makeQuery(id+"F0.imprint","INTERSECT",VERTEX,{"derivedFrom":[subQ1,subQ3]});Q63=makeQuery(id+"F0.imprint","IMPRINT",FACE,{"disambiguationData":[TD([[makeQuery(id+"F0.imprint","IMPRINT",EDGE,{"disambiguationData":[TD([[subQ4,1.0]])],"derivedFrom":subQ3}),1.0]])]});}
            var Q64;
            {var subQ0=sQuery(id+"F0.wireOp",EDGE,"E47");var subQ1=sQuery(id+"F0.wireOp",EDGE,"E1");var subQ2=makeQuery(id+"F0.imprint","INTERSECT",VERTEX,{"derivedFrom":[subQ1,subQ0]});Q64=makeQuery(id+"F0.imprint","IMPRINT",FACE,{"disambiguationData":[TD([[makeQuery(id+"F0.imprint","IMPRINT",EDGE,{"disambiguationData":[TD([[subQ2,-1.0]])],"derivedFrom":subQ1}),-1.0]])]});}
            var Q65;
            {var subQ0=sQuery(id+"F0.wireOp",EDGE,"E28");var subQ1=sQuery(id+"F0.wireOp",EDGE,"E1");var subQ2=makeQuery(id+"F0.imprint","INTERSECT",VERTEX,{"derivedFrom":[subQ1,subQ0]});Q65=makeQuery(id+"F0.imprint","IMPRINT",FACE,{"disambiguationData":[TD([[makeQuery(id+"F0.imprint","IMPRINT",EDGE,{"disambiguationData":[TD([[subQ2,-1.0]])],"derivedFrom":subQ1}),-1.0]])]});}
            var Q66;
            {var subQ1=sQuery(id+"F0.wireOp",EDGE,"E2");var subQ3=sQuery(id+"F0.wireOp",EDGE,"E43");var subQ4=makeQuery(id+"F0.imprint","INTERSECT",VERTEX,{"derivedFrom":[subQ1,subQ3]});Q66=makeQuery(id+"F0.imprint","IMPRINT",FACE,{"disambiguationData":[TD([[makeQuery(id+"F0.imprint","IMPRINT",EDGE,{"disambiguationData":[TD([[subQ4,1.0]])],"derivedFrom":subQ3}),1.0]])]});}
            var Q67;
            {var subQ0=sQuery(id+"F0.wireOp",EDGE,"E34");var subQ1=sQuery(id+"F0.wireOp",EDGE,"E2");var subQ2=makeQuery(id+"F0.imprint","INTERSECT",VERTEX,{"derivedFrom":[subQ1,subQ0]});Q67=makeQuery(id+"F0.imprint","IMPRINT",FACE,{"disambiguationData":[TD([[makeQuery(id+"F0.imprint","IMPRINT",EDGE,{"disambiguationData":[TD([[subQ2,-1.0]])],"derivedFrom":subQ0}),1.0]])]});}
            var Q68;
            {var subQ0=sQuery(id+"F0.wireOp",EDGE,"E40");var subQ1=sQuery(id+"F0.wireOp",EDGE,"E1");var subQ2=makeQuery(id+"F0.imprint","INTERSECT",VERTEX,{"derivedFrom":[subQ1,subQ0]});Q68=makeQuery(id+"F0.imprint","IMPRINT",FACE,{"disambiguationData":[TD([[makeQuery(id+"F0.imprint","IMPRINT",EDGE,{"disambiguationData":[TD([[subQ2,-1.0]])],"derivedFrom":subQ1}),-1.0]])]});}
            var Q69;
            {var subQ0=sQuery(id+"F0.wireOp",EDGE,"E43");var subQ1=sQuery(id+"F0.wireOp",EDGE,"E1");var subQ2=makeQuery(id+"F0.imprint","INTERSECT",VERTEX,{"derivedFrom":[subQ1,subQ0]});Q69=makeQuery(id+"F0.imprint","IMPRINT",FACE,{"disambiguationData":[TD([[makeQuery(id+"F0.imprint","IMPRINT",EDGE,{"disambiguationData":[TD([[subQ2,-1.0]])],"derivedFrom":subQ1}),-1.0]])]});}
            var Q70;
            {var subQ0=sQuery(id+"F0.wireOp",EDGE,"E45");var subQ1=sQuery(id+"F0.wireOp",EDGE,"E1");var subQ2=makeQuery(id+"F0.imprint","INTERSECT",VERTEX,{"derivedFrom":[subQ1,subQ0]});Q70=makeQuery(id+"F0.imprint","IMPRINT",FACE,{"disambiguationData":[TD([[makeQuery(id+"F0.imprint","IMPRINT",EDGE,{"disambiguationData":[TD([[subQ2,-1.0]])],"derivedFrom":subQ1}),-1.0]])]});}
            var Q71;
            {var subQ0=sQuery(id+"F0.wireOp",EDGE,"E32");var subQ1=sQuery(id+"F0.wireOp",EDGE,"E2");var subQ2=makeQuery(id+"F0.imprint","INTERSECT",VERTEX,{"derivedFrom":[subQ1,subQ0]});Q71=makeQuery(id+"F0.imprint","IMPRINT",FACE,{"disambiguationData":[TD([[makeQuery(id+"F0.imprint","IMPRINT",EDGE,{"disambiguationData":[TD([[subQ2,-1.0]])],"derivedFrom":subQ0}),1.0]])]});}
            var Q72;
            {var subQ0=sQuery(id+"F0.wireOp",EDGE,"E41");var subQ1=sQuery(id+"F0.wireOp",EDGE,"E1");var subQ2=makeQuery(id+"F0.imprint","INTERSECT",VERTEX,{"derivedFrom":[subQ1,subQ0]});Q72=makeQuery(id+"F0.imprint","IMPRINT",FACE,{"disambiguationData":[TD([[makeQuery(id+"F0.imprint","IMPRINT",EDGE,{"disambiguationData":[TD([[subQ2,-1.0]])],"derivedFrom":subQ1}),-1.0]])]});}
            var Q73;
            {var subQ1=sQuery(id+"F0.wireOp",EDGE,"E2");var subQ3=sQuery(id+"F0.wireOp",EDGE,"E45");var subQ4=makeQuery(id+"F0.imprint","INTERSECT",VERTEX,{"derivedFrom":[subQ1,subQ3]});Q73=makeQuery(id+"F0.imprint","IMPRINT",FACE,{"disambiguationData":[TD([[makeQuery(id+"F0.imprint","IMPRINT",EDGE,{"disambiguationData":[TD([[subQ4,1.0]])],"derivedFrom":subQ3}),1.0]])]});}
            var Q74;
            {var subQ0=sQuery(id+"F0.wireOp",EDGE,"E59");var subQ1=sQuery(id+"F0.wireOp",EDGE,"E15");var subQ2=makeQuery(id+"F0.imprint","INTERSECT",VERTEX,{"derivedFrom":[subQ1,subQ0]});Q74=makeQuery(id+"F0.imprint","IMPRINT",FACE,{"disambiguationData":[TD([[makeQuery(id+"F0.imprint","IMPRINT",EDGE,{"disambiguationData":[TD([[subQ2,-1.0]])],"derivedFrom":subQ1}),-1.0]])]});}
            var Q75;
            {var subQ0=sQuery(id+"F0.wireOp",EDGE,"E68");var subQ1=sQuery(id+"F0.wireOp",EDGE,"E8");var subQ2=makeQuery(id+"F0.imprint","INTERSECT",VERTEX,{"derivedFrom":[subQ1,subQ0]});Q75=makeQuery(id+"F0.imprint","IMPRINT",FACE,{"disambiguationData":[TD([[makeQuery(id+"F0.imprint","IMPRINT",EDGE,{"disambiguationData":[TD([[subQ2,-1.0]])],"derivedFrom":subQ1}),-1.0]])]});}
            var Q76;
            {var subQ0=sQuery(id+"F0.wireOp",EDGE,"E68");var subQ1=sQuery(id+"F0.wireOp",EDGE,"E8");var subQ2=makeQuery(id+"F0.imprint","INTERSECT",VERTEX,{"derivedFrom":[subQ1,subQ0]});Q76=makeQuery(id+"F0.imprint","IMPRINT",FACE,{"disambiguationData":[TD([[makeQuery(id+"F0.imprint","IMPRINT",EDGE,{"disambiguationData":[TD([[subQ2,-1.0]])],"derivedFrom":subQ1}),1.0]])]});}
            var Q77;
            {var subQ0=sQuery(id+"F0.wireOp",EDGE,"E61");var subQ1=sQuery(id+"F0.wireOp",EDGE,"E15");var subQ2=makeQuery(id+"F0.imprint","INTERSECT",VERTEX,{"derivedFrom":[subQ1,subQ0]});Q77=makeQuery(id+"F0.imprint","IMPRINT",FACE,{"disambiguationData":[TD([[makeQuery(id+"F0.imprint","IMPRINT",EDGE,{"disambiguationData":[TD([[subQ2,1.0]])],"derivedFrom":subQ1}),-1.0]])]});}
            var Q78;
            {var subQ0=sQuery(id+"F0.wireOp",EDGE,"E61");var subQ1=sQuery(id+"F0.wireOp",EDGE,"E16");var subQ2=makeQuery(id+"F0.imprint","INTERSECT",VERTEX,{"derivedFrom":[subQ1,subQ0]});Q78=makeQuery(id+"F0.imprint","IMPRINT",FACE,{"disambiguationData":[TD([[makeQuery(id+"F0.imprint","IMPRINT",EDGE,{"disambiguationData":[TD([[subQ2,-1.0]])],"derivedFrom":subQ1}),-1.0]])]});}
            var Q79;
            {var subQ0=sQuery(id+"F0.wireOp",EDGE,"E60");var subQ1=sQuery(id+"F0.wireOp",EDGE,"E16");var subQ2=makeQuery(id+"F0.imprint","INTERSECT",VERTEX,{"derivedFrom":[subQ1,subQ0]});Q79=makeQuery(id+"F0.imprint","IMPRINT",FACE,{"disambiguationData":[TD([[makeQuery(id+"F0.imprint","IMPRINT",EDGE,{"disambiguationData":[TD([[subQ2,1.0]])],"derivedFrom":subQ1}),-1.0]])]});}
            var Q80;
            {var subQ0=sQuery(id+"F0.wireOp",EDGE,"E22");var subQ1=sQuery(id+"F0.wireOp",EDGE,"E17");var subQ2=makeQuery(id+"F0.imprint","INTERSECT",VERTEX,{"derivedFrom":[subQ1,subQ0]});Q80=makeQuery(id+"F0.imprint","IMPRINT",FACE,{"disambiguationData":[TD([[makeQuery(id+"F0.imprint","IMPRINT",EDGE,{"disambiguationData":[TD([[subQ2,1.0]])],"derivedFrom":subQ1}),-1.0]])]});}
            var Q81;
            {var subQ0=sQuery(id+"F0.wireOp",EDGE,"E70");var subQ1=sQuery(id+"F0.wireOp",EDGE,"E6");var subQ2=makeQuery(id+"F0.imprint","INTERSECT",VERTEX,{"derivedFrom":[subQ1,subQ0]});Q81=makeQuery(id+"F0.imprint","IMPRINT",FACE,{"disambiguationData":[TD([[makeQuery(id+"F0.imprint","IMPRINT",EDGE,{"disambiguationData":[TD([[subQ2,-1.0]])],"derivedFrom":subQ1}),-1.0]])]});}
            var Q82;
            {var subQ0=sQuery(id+"F0.wireOp",EDGE,"E70");var subQ1=sQuery(id+"F0.wireOp",EDGE,"E6");var subQ2=makeQuery(id+"F0.imprint","INTERSECT",VERTEX,{"derivedFrom":[subQ1,subQ0]});Q82=makeQuery(id+"F0.imprint","IMPRINT",FACE,{"disambiguationData":[TD([[makeQuery(id+"F0.imprint","IMPRINT",EDGE,{"disambiguationData":[TD([[subQ2,-1.0]])],"derivedFrom":subQ1}),1.0]])]});}
            var Q83;
            {var subQ0=sQuery(id+"F0.wireOp",EDGE,"E26");var subQ1=sQuery(id+"F0.wireOp",EDGE,"E17");var subQ2=makeQuery(id+"F0.imprint","INTERSECT",VERTEX,{"derivedFrom":[subQ1,subQ0]});Q83=makeQuery(id+"F0.imprint","IMPRINT",FACE,{"disambiguationData":[TD([[makeQuery(id+"F0.imprint","IMPRINT",EDGE,{"disambiguationData":[TD([[subQ2,-1.0]])],"derivedFrom":subQ1}),-1.0]])]});}
            var Q84;
            {var subQ0=sQuery(id+"F0.wireOp",EDGE,"E21");var subQ1=sQuery(id+"F0.wireOp",EDGE,"E18");var subQ2=makeQuery(id+"F0.imprint","INTERSECT",VERTEX,{"derivedFrom":[subQ1,subQ0]});Q84=makeQuery(id+"F0.imprint","IMPRINT",FACE,{"disambiguationData":[TD([[makeQuery(id+"F0.imprint","IMPRINT",EDGE,{"disambiguationData":[TD([[subQ2,1.0]])],"derivedFrom":subQ1}),1.0]])]});}
            var Q85;
            {var subQ0=sQuery(id+"F0.wireOp",EDGE,"E24");var subQ1=sQuery(id+"F0.wireOp",EDGE,"E18");var subQ2=makeQuery(id+"F0.imprint","INTERSECT",VERTEX,{"derivedFrom":[subQ1,subQ0]});Q85=makeQuery(id+"F0.imprint","IMPRINT",FACE,{"disambiguationData":[TD([[makeQuery(id+"F0.imprint","IMPRINT",EDGE,{"disambiguationData":[TD([[subQ2,-1.0]])],"derivedFrom":subQ1}),1.0]])]});}
            var Q86;
            {var subQ0=sQuery(id+"F0.wireOp",EDGE,"E25");var subQ1=sQuery(id+"F0.wireOp",EDGE,"E20");var subQ2=makeQuery(id+"F0.imprint","INTERSECT",VERTEX,{"derivedFrom":[subQ1,subQ0]});Q86=makeQuery(id+"F0.imprint","IMPRINT",FACE,{"disambiguationData":[TD([[makeQuery(id+"F0.imprint","IMPRINT",EDGE,{"disambiguationData":[TD([[subQ2,1.0]])],"derivedFrom":subQ1}),1.0]])]});}
            var Q87;
            {var subQ0=sQuery(id+"F0.wireOp",EDGE,"E23");var subQ1=sQuery(id+"F0.wireOp",EDGE,"E20");var subQ2=makeQuery(id+"F0.imprint","INTERSECT",VERTEX,{"derivedFrom":[subQ1,subQ0]});Q87=makeQuery(id+"F0.imprint","IMPRINT",FACE,{"disambiguationData":[TD([[makeQuery(id+"F0.imprint","IMPRINT",EDGE,{"disambiguationData":[TD([[subQ2,-1.0]])],"derivedFrom":subQ1}),1.0]])]});}
            var Q88;
            {var subQ0=sQuery(id+"F0.wireOp",EDGE,"E22");var subQ1=sQuery(id+"F0.wireOp",EDGE,"E19");var subQ2=makeQuery(id+"F0.imprint","INTERSECT",VERTEX,{"derivedFrom":[subQ1,subQ0]});Q88=makeQuery(id+"F0.imprint","IMPRINT",FACE,{"disambiguationData":[TD([[makeQuery(id+"F0.imprint","IMPRINT",EDGE,{"disambiguationData":[TD([[subQ2,1.0]])],"derivedFrom":subQ1}),1.0]])]});}
            var Q89;
            {var subQ0=sQuery(id+"F0.wireOp",EDGE,"E26");var subQ1=sQuery(id+"F0.wireOp",EDGE,"E19");var subQ2=makeQuery(id+"F0.imprint","INTERSECT",VERTEX,{"derivedFrom":[subQ1,subQ0]});Q89=makeQuery(id+"F0.imprint","IMPRINT",FACE,{"disambiguationData":[TD([[makeQuery(id+"F0.imprint","IMPRINT",EDGE,{"disambiguationData":[TD([[subQ2,-1.0]])],"derivedFrom":subQ1}),1.0]])]});}
            extrude(context, id + "F1", {"entities" : qUnion([Q0, Q1, Q2, Q3, Q4, Q5, Q6, Q7, Q8, Q9, Q10, Q11, Q12, Q13, Q14, Q15, Q16, Q17, Q18, Q19, Q20, Q21, Q22, Q23, Q24, Q25, Q26, Q27, Q28, Q29, Q30, Q31, Q32, Q33, Q34, Q35, Q36, Q37, Q38, Q39, Q40, Q41, Q42, Q43, Q44, Q45, Q46, Q47, Q48, Q49, Q50, Q51, Q52, Q53, Q54, Q55, Q56, Q57, Q58, Q59, Q60, Q61, Q62, Q63, Q64, Q65, Q66, Q67, Q68, Q69, Q70, Q71, Q72, Q73, Q74, Q75, Q76, Q77, Q78, Q79, Q80, Q81, Q82, Q83, Q84, Q85, Q86, Q87, Q88, Q89]), "depth" : 7.04 * mm, "offsetDistance" : 25.4 * mm});
        }
    });
